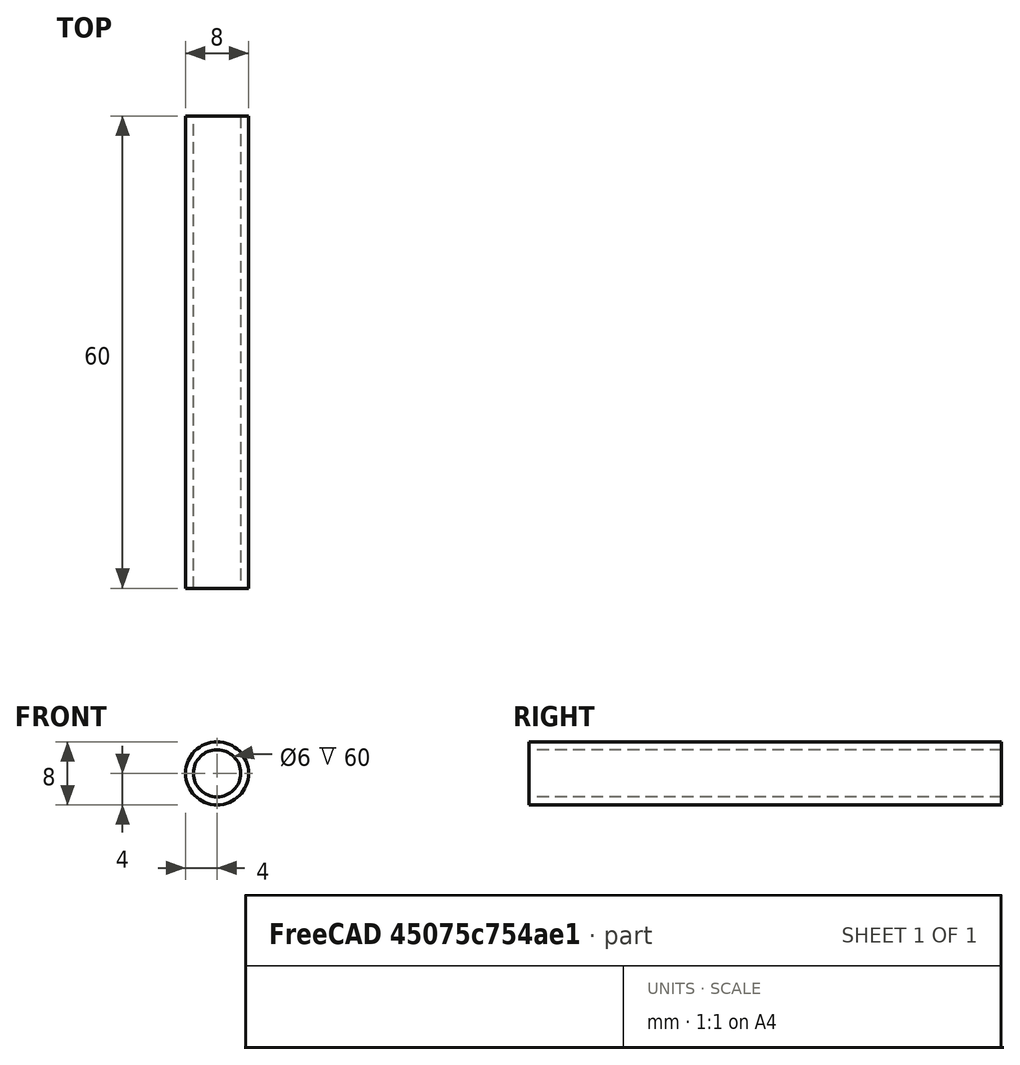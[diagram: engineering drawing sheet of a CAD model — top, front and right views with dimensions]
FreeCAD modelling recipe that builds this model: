
FCSTD DOCUMENT  (FreeCAD 0.18.4R)
Label: tube
Comment: # 2020-02-12 13:38:20: read from <userpath>/repositories/sussex_neuro/Olfactometer/hardware/mechanics/from_raiser_et_al/tube.ipt
License: All rights reserved
LicenseURL: http://en.wikipedia.org/wiki/All_rights_reserved
objects: Sketcher::SketchObject×2, Spreadsheet::Sheet×1, Part::Extrusion×1
note: 3 computed .brp shape members not serialized (recipe doc carries the construction recipe); baked Part::Feature solids carry a one-line shape summary decoded from their .brp

FEATURE [Spreadsheet::Sheet] Parameters
  cells = A1=Parameter; B1=Value; C1=Fromula; D1=Tolerance; E1=Comment; A2=d10; B2(d10_)=0.3; C2=0.3mm; D2=NOMINAL; A3=d11; B3(d11_)=0.3; C3=0.3mm; D3=NOMINAL; A4=d12; B4(d12_)=0.5; C4=0.5mm; D4=NOMINAL; A5=d13; B5(d13_)=2; C5=2mm; D5=NOMINAL; A6=d14; B6(d14_)=0; C6=0mm; D6=NOMINAL; A7=d15; B7(d15_)=20; C7=20mm; D7=NOMINAL; A8=d4; B8(d4_)=8; C8=8mm; D8=NOMINAL; A9=d6; B9(d6_)=6.000000000000001; C9=6mm; D9=NOMINAL; A10=d7; B10(d7_)=60; C10=60mm; D10=NOMINAL; A11=d8; B11(d8_)=0; C11=0°; D11=NOMINAL; A12=d9; B12(d9_)=0.3; C12=0.3mm; D12=NOMINAL
FEATURE [Sketcher::SketchObject] Sketch3
  Placement = pos=(0,0,0) rot=(0,0.707107,0.707107;3.14159rad)
  sketch-geometry (2):
    g0: Circle CenterX=0 CenterY=0 CenterZ=0 NormalX=0 NormalY=0 NormalZ=1 AngleXU=0 Radius=4
    g1: Circle CenterX=0 CenterY=0 CenterZ=0 NormalX=0 NormalY=0 NormalZ=1 AngleXU=0 Radius=3
  constraints (2):
    c: Radius(g0) = 4  'd4'
    c: Radius(g1) = 3  'd6'
FEATURE [Sketcher::SketchObject] Sketch3_bp
  Placement = pos=(0,0,0) rot=(0,0.707107,0.707107;3.14159rad)
  sketch-geometry (2):
    g0: Circle CenterX=0 CenterY=0 CenterZ=0 NormalX=0 NormalY=0 NormalZ=1 AngleXU=0 Radius=4
    g1: Circle CenterX=0 CenterY=0 CenterZ=0 NormalX=0 NormalY=0 NormalZ=1 AngleXU=0 Radius=3
FEATURE [Part::Extrusion] Extrusion2
  Base = -> Sketch3_bp
  Dir = (0,1,0)
  DirMode = 0
  FaceMakerClass = Part::FaceMakerBullseye
  LengthFwd = 60
  LengthRev = 0
  Solid = true
  Symmetric = false
  expr: LengthFwd = Parameters.d7_
  expr: TaperAngle = Parameters.d8_
